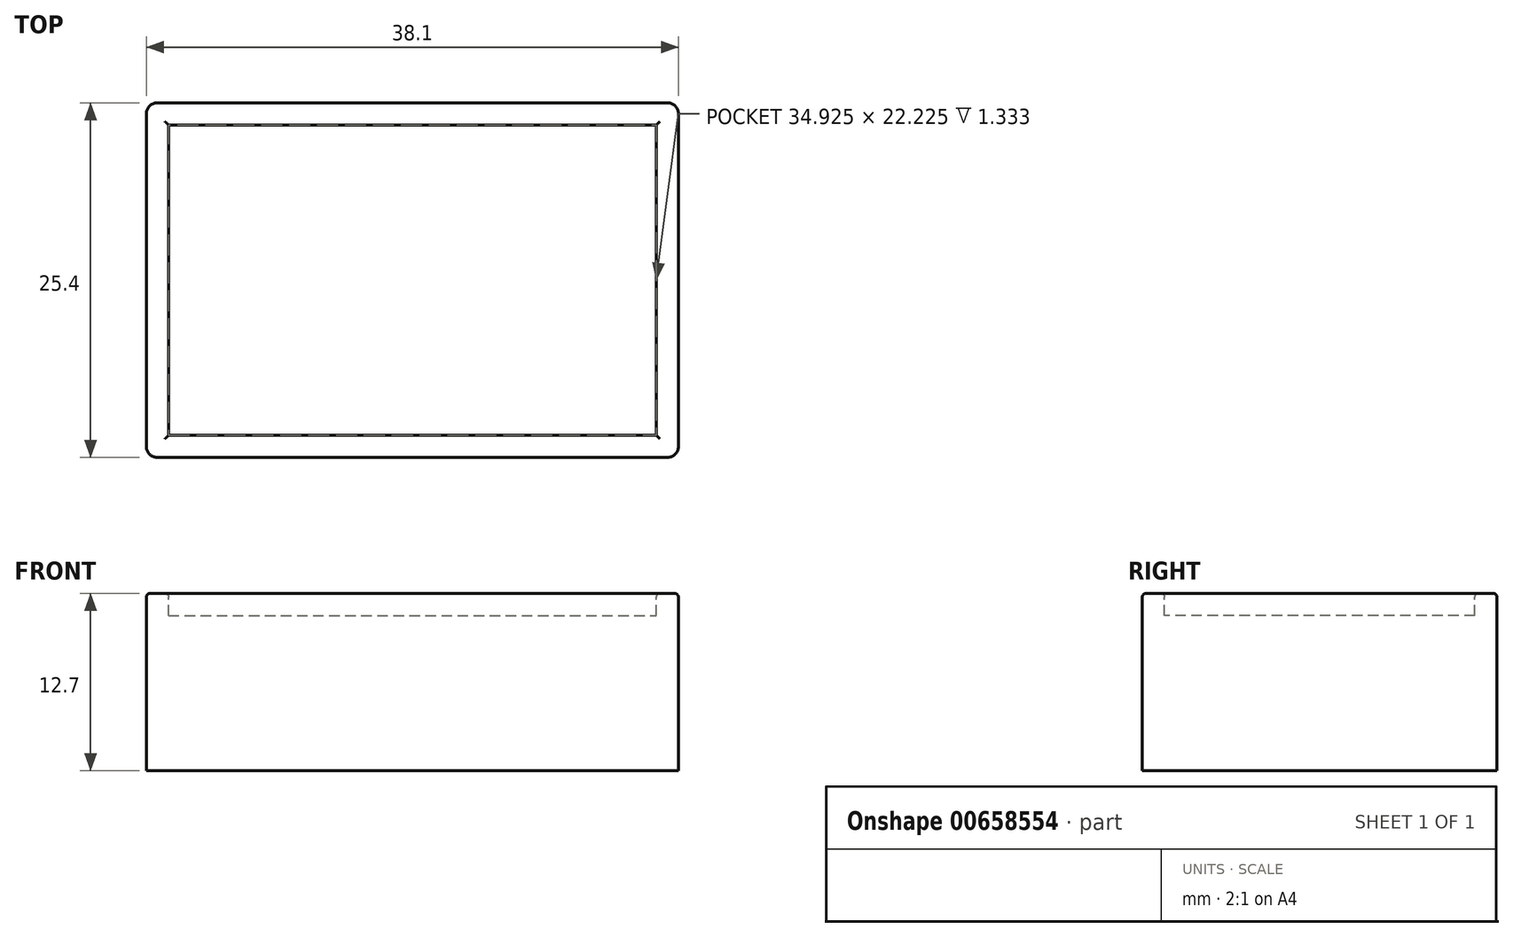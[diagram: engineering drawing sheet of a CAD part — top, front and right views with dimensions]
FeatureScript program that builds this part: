
annotation { "Feature Type Name" : "Feature", "Feature Type Description" : "" }
export const myFeature = defineFeature(function(context is Context, id is Id, definition is map)
    precondition{}
    {
        {
            var Q0;
            Q0=qCreatedBy(makeId("Top.planeOp"),FACE);
            var sketch = newSketch(context, id + "F0", { "sketchPlane" : qUnion([Q0])});
            skLineSegment(sketch, "E0.bottom", {"start": v(-19.05, 12.7) * mm, "end": v(19.05, 12.7) * mm});
            skLineSegment(sketch, "E0.top", {"start": v(-19.05, -12.7) * mm, "end": v(19.05, -12.7) * mm});
            skLineSegment(sketch, "E0.left", {"start": v(-19.05, 12.7) * mm, "end": v(-19.05, -12.7) * mm});
            skLineSegment(sketch, "E0.right", {"start": v(19.05, 12.7) * mm, "end": v(19.05, -12.7) * mm});
            skSolve(sketch);
        }
        {
            var Q0;
            Q0=qSketchRegion(id+"F0",true);
            extrude(context, id + "F1", {"entities" : qUnion([Q0]), "depth" : 12.7 * mm, "offsetDistance" : 25.4 * mm});
        }
        {
            var Q0;
            Q0=makeQuery(id+"F1.opExtrude","CAP_FACE",FACE,{"disambiguationData":[OSD([sQuery(id+"F0.wireOp",EDGE,"E0.bottom"),sQuery(id+"F0.wireOp",EDGE,"E0.top"),sQuery(id+"F0.wireOp",EDGE,"E0.left"),sQuery(id+"F0.wireOp",EDGE,"E0.right")])],"isStart":false});
            var sketch = newSketch(context, id + "F2", { "sketchPlane" : qUnion([Q0])});
            skLineSegment(sketch, "E1.bottom", {"start": v(-17.46, 11.11) * mm, "end": v(17.46, 11.11) * mm});
            skLineSegment(sketch, "E1.top", {"start": v(-17.46, -11.11) * mm, "end": v(17.46, -11.11) * mm});
            skLineSegment(sketch, "E1.left", {"start": v(-17.46, 11.11) * mm, "end": v(-17.46, -11.11) * mm});
            skLineSegment(sketch, "E1.right", {"start": v(17.46, 11.11) * mm, "end": v(17.46, -11.11) * mm});
            skSolve(sketch);
        }
        {
            var Q0;
            Q0=qSketchRegion(id+"F2",true);
            extrude(context, id + "F3", {"entities" : qUnion([Q0]), "operationType" : NewBodyOperationType.REMOVE, "oppositeDirection" : true, "depth" : 1.59 * mm, "offsetDistance" : 25.4 * mm});
        }
        {
            var Q0;
            Q0=makeQuery(id+"F1.opExtrude","SWEPT_EDGE",EDGE,{"disambiguationData":[OSD([sQuery(id+"F0.wireOp",EDGE,"E0.top"),sQuery(id+"F0.wireOp",EDGE,"E0.left")])]});
            var Q1;
            Q1=makeQuery(id+"F1.opExtrude","SWEPT_EDGE",EDGE,{"disambiguationData":[OSD([sQuery(id+"F0.wireOp",EDGE,"E0.bottom"),sQuery(id+"F0.wireOp",EDGE,"E0.left")])]});
            var Q2;
            Q2=makeQuery(id+"F1.opExtrude","SWEPT_EDGE",EDGE,{"disambiguationData":[OSD([sQuery(id+"F0.wireOp",EDGE,"E0.bottom"),sQuery(id+"F0.wireOp",EDGE,"E0.right")])]});
            var Q3;
            Q3=makeQuery(id+"F1.opExtrude","SWEPT_EDGE",EDGE,{"disambiguationData":[OSD([sQuery(id+"F0.wireOp",EDGE,"E0.top"),sQuery(id+"F0.wireOp",EDGE,"E0.right")])]});
            fillet(context, id + "F4", {"entities" : qUnion([Q0, Q1, Q2, Q3]), "radius" : 0.76 * mm, "tangentPropagation" : true, "allowEdgeOverflow" : false});
        }
        {
            var Q0;
            Q0=makeQuery(id+"F1.opExtrude","CAP_FACE",FACE,{"disambiguationData":[OSD([sQuery(id+"F0.wireOp",EDGE,"E0.bottom"),sQuery(id+"F0.wireOp",EDGE,"E0.top"),sQuery(id+"F0.wireOp",EDGE,"E0.left"),sQuery(id+"F0.wireOp",EDGE,"E0.right")])],"isStart":false});
            fillet(context, id + "F5", {"entities" : qUnion([Q0]), "radius" : 0.25 * mm, "tangentPropagation" : true, "allowEdgeOverflow" : false});
        }
    });
